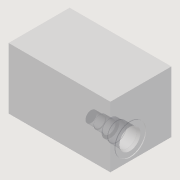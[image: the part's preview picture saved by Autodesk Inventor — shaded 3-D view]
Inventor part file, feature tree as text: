
AUTODESK INVENTOR PART (.ipt)
format: ipt  version: 2014 (Build 180170000, 170)  size: 199,168 bytes
history: native  units: mm
features: other x48, extrude x22, sketch x22
ambient origin geometry x8: Origin, YZ Plane, XZ Plane, XY Plane, X Axis, Y Axis, Z Axis, Center Point
bodies: 实体1 (feature_tree)
feature tree (92):
  extrude  "拉伸1"  Depth=30.2mm
  other  "UCS1"
  other  "UCS2"
  other  "UCS3"
  other  "UCS4"
  other  "UCS5"
  other  "UCS6"
  extrude  "拉伸2"  Depth=70.0mm
  extrude  "拉伸3"  Depth=0.79mm
  extrude  "拉伸5"  Depth=22.22mm
  extrude  "拉伸6"  Depth=14.28mm
  extrude  "拉伸7"  Depth=16.5mm TaperAngle=0.0deg
  extrude  "拉伸8"  Depth=38.5mm TaperAngle=0.0deg
  extrude  "拉伸9"  Depth=17.5mm
  extrude  "拉伸10"  Depth=47.63mm
  extrude  "拉伸11"  Depth=63.5mm TaperAngle=0.0deg
  extrude  "拉伸12"  Depth=30.2mm
  extrude  "拉伸13"  Depth=20.0mm
  extrude  "拉伸14"  Depth=0.79mm
  extrude  "拉伸15"  Depth=2.74mm
  extrude  "拉伸16"  Depth=12.7mm TaperAngle=0.0deg
  extrude  "拉伸17"  Depth=60.0mm TaperAngle=0.0deg
  extrude  "拉伸18"  Depth=60.0mm
  extrude  "拉伸19"  Depth=12.7mm
  extrude  "拉伸20"  Depth=60.0mm TaperAngle=0.0deg
  extrude  "拉伸21"  Depth=60.0mm
  extrude  "拉伸22"  Depth=60.0mm
  extrude  "拉伸23"  Depth=38.1mm TaperAngle=0.0deg
  sketch  "草图1"  dims[d0=60.0mm d1=0.0mm]
  sketch  "草图2"  dims[d2=0.0mm d3=0.0mm d4=0.0mm d5=0.0mm d6=0.0mm d7=0.0mm]
  sketch  "草图3"  dims[d8=0.0mm d9=0.0mm d10=0.0mm d11=0.0mm d12=0.0mm d13=0.0mm]
  sketch  "草图6"  dims[d14=0.0mm d15=0.0mm d16=0.0mm d17=0.0mm d18=0.0mm d19=0.0mm]
  sketch  "草图7"  dims[d20=0.0mm d21=0.0mm d22=0.0mm d23=0.0mm d24=0.0mm d25=0.0mm]
  sketch  "草图8"  dims[d26=0.0mm d27=0.0mm d28=0.0mm d29=0.0mm d30=0.0mm d31=0.0mm]
  sketch  "草图9"  dims[d32=0.0mm d33=0.0mm d34=0.0mm d35=0.0mm d36=0.0mm d37=0.0mm d38=30.2mm]
  sketch  "草图10"  dims[d39=80.0mm d40=70.0mm]
  sketch  "草图11"  dims[d41=0.79mm d42=0.0mm d43=24.0mm]
  sketch  "草图12"  dims[d44=2.74mm d45=-2.617994mm d49=22.22mm]
  sketch  "草图13"  dims[d50=14.28mm d51=0.0mm d52=14.28mm d53=-7.853982mm]
  sketch  "草图14"  dims[d54=20.63mm d55=16.5mm d56=0.0mm]
  sketch  "草图16"  dims[d57=19.08mm d58=38.5mm d59=0.0mm]
  sketch  "草图17"  dims[d60=38.5mm d61=-5.235988mm d62=17.5mm]
  sketch  "草图18"  dims[d63=47.63mm d64=0.0mm d65=47.63mm d66=-10.471976mm]
  sketch  "草图19"  dims[d67=15.0mm d68=63.5mm d69=0.0mm]
  sketch  "草图20"  dims[d70=63.5mm d71=-10.297443mm d75=30.2mm]
  sketch  "草图21"  dims[d76=18.0mm d77=20.0mm]
  sketch  "草图22"  dims[d78=0.79mm d79=0.0mm d80=20.7mm]
  sketch  "草图23"  dims[d81=2.74mm d82=-2.617994mm d83=2.74mm d84=-7.853982mm]
  sketch  "草图24"  dims[d85=19.05mm d86=12.7mm d87=0.0mm]
  sketch  "草图25"  dims[d88=17.48mm d89=19.05mm d90=0.0mm d91=19.05mm d92=-10.471976mm d93=12.7mm d94=29.3mm d95=0.0mm d96=29.3mm d97=-10.471976mm d98=11.0mm d99=38.1mm d100=0.0mm d101=38.1mm d102=-10.297443mm d106=100.0mm d107=60.0mm]
  other  "UCS1: YZ 平面"
  other  "UCS1: XZ 平面"
  other  "UCS1: XY 平面"
  other  "UCS1: X 轴"
  other  "UCS1: Y 轴"
  other  "UCS1: Z 轴"
  other  "UCS1: 原点"
  other  "UCS2: YZ 平面"
  other  "UCS2: XZ 平面"
  other  "UCS2: XY 平面"
  other  "UCS2: X 轴"
  other  "UCS2: Y 轴"
  other  "UCS2: Z 轴"
  other  "UCS2: 原点"
  other  "UCS3: YZ 平面"
  other  "UCS3: XZ 平面"
  other  "UCS3: XY 平面"
  other  "UCS3: X 轴"
  other  "UCS3: Y 轴"
  other  "UCS3: Z 轴"
  other  "UCS3: 原点"
  other  "UCS4: YZ 平面"
  other  "UCS4: XZ 平面"
  other  "UCS4: XY 平面"
  other  "UCS4: X 轴"
  other  "UCS4: Y 轴"
  other  "UCS4: Z 轴"
  other  "UCS4: 原点"
  other  "UCS5: YZ 平面"
  other  "UCS5: XZ 平面"
  other  "UCS5: XY 平面"
  other  "UCS5: X 轴"
  other  "UCS5: Y 轴"
  other  "UCS5: Z 轴"
  other  "UCS5: 原点"
  other  "UCS6: YZ 平面"
  other  "UCS6: XZ 平面"
  other  "UCS6: XY 平面"
  other  "UCS6: X 轴"
  other  "UCS6: Y 轴"
  other  "UCS6: Z 轴"
  other  "UCS6: 原点"
